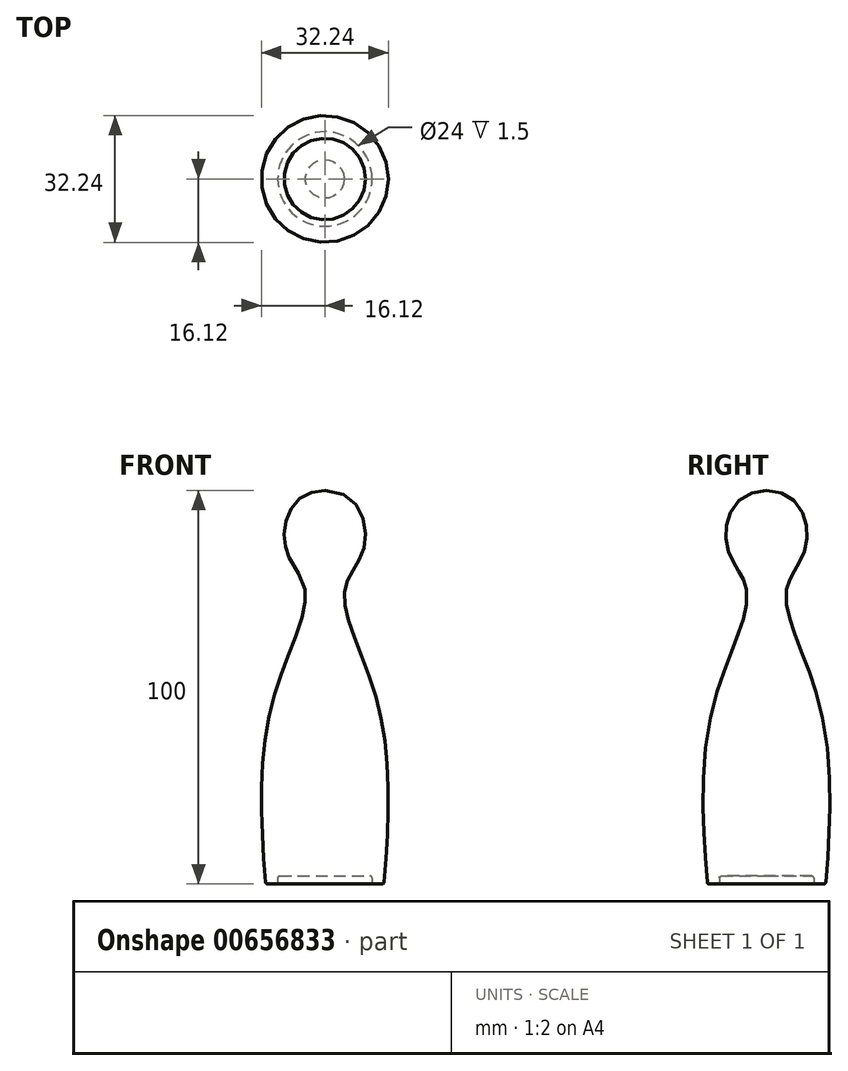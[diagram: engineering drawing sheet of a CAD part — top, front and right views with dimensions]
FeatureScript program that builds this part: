
annotation { "Feature Type Name" : "Feature", "Feature Type Description" : "" }
export const myFeature = defineFeature(function(context is Context, id is Id, definition is map)
    precondition{}
    {
        {
            var Q0;
            Q0=qCreatedBy(makeId("Front.planeOp"),FACE);
            var sketch = newSketch(context, id + "F0", { "sketchPlane" : qUnion([Q0])});
            skLineSegment(sketch, "E0", {"start": v(0, 53.24) * mm, "end": v(0, -46.52) * mm, "construction": true});
            skFitSpline(sketch, "E1", {"points": [v(0, 48.43) * mm, v(10.08, 34.43) * mm, v(5, 22.85) * mm, v(13.2, -4.93) * mm, v(15, -51.57) * mm], "startDerivative": vector(127.18, -1.17) * mm, "endDerivative": vector(-12.23, -138.3) * mm});
            skLineSegment(sketch, "E2", {"start": v(15, -51.57) * mm, "end": v(0, -51.57) * mm});
            skLineSegment(sketch, "E3", {"start": v(0, 48.43) * mm, "end": v(0, -51.57) * mm});
            skPoint(sketch, "E4", {"position": v(15.75, -20.25) * mm});
            skPoint(sketch, "E5", {"position": v(10, 40.23) * mm});
            skSolve(sketch);
        }
        {
            var Q0;
            Q0=makeQuery(id+"F0.imprint","IMPRINT",FACE,{"disambiguationData":[TD([[makeQuery(id+"F0.imprint","IMPRINT",EDGE,{"derivedFrom":sQuery(id+"F0.wireOp",EDGE,"E1")}),-1.0]])]});
            var Q1;
            Q1=sQuery(id+"F0.wireOp",EDGE,"E3");
            revolve(context, id + "F1", {"entities" : qUnion([Q0]), "axis" : qUnion([Q1]), "revolveType" : RevolveType.FULL});
        }
        {
            var Q0;
            Q0=makeQuery(id+"F1.opRevolve","SWEPT_FACE",FACE,{"disambiguationData":[OSD([sQuery(id+"F0.wireOp",EDGE,"E2")])]});
            var sketch = newSketch(context, id + "F2", { "sketchPlane" : qUnion([Q0])});
            skCircle(sketch, "E6", {"center": v(0, 0) * mm, "radius": 12 * mm});
            skSolve(sketch);
        }
        {
            var Q0;
            Q0=makeQuery(id+"F2.imprint","IMPRINT",FACE,{"disambiguationData":[TD([[makeQuery(id+"F2.imprint","IMPRINT",EDGE,{"derivedFrom":sQuery(id+"F2.wireOp",EDGE,"E6")}),1.0]])]});
            var Q1;
            Q1=sQuery(id+"F2.wireOp",EDGE,"E6");
            extrude(context, id + "F3", {"entities" : qUnion([Q0]), "operationType" : NewBodyOperationType.REMOVE, "surfaceEntities" : qUnion([Q1]), "oppositeDirection" : true, "depth" : 2 * mm, "offsetDistance" : 25 * mm});
        }
        {
            var Q0;
            Q0=makeQuery(id+"F3.boolean.opBoolean","COPY",EDGE,{"derivedFrom":makeQuery(id+"F3.opExtrude","CAP_EDGE",EDGE,{"disambiguationData":[OSD([sQuery(id+"F2.wireOp",EDGE,"E6")])],"isStart":true})});
            var Q1;
            Q1=makeQuery(id+"F1.opRevolve","SWEPT_EDGE",EDGE,{"disambiguationData":[OSD([sQuery(id+"F0.wireOp",EDGE,"E1"),sQuery(id+"F0.wireOp",EDGE,"E2")])]});
            var Q2;
            Q2=makeQuery(id+"F3.boolean.opBoolean","COPY",EDGE,{"derivedFrom":makeQuery(id+"F3.opExtrude","CAP_EDGE",EDGE,{"disambiguationData":[OSD([sQuery(id+"F2.wireOp",EDGE,"E6")])],"isStart":false})});
            fillet(context, id + "F4", {"entities" : qUnion([Q0, Q1, Q2]), "radius" : 0.5 * mm, "tangentPropagation" : true, "allowEdgeOverflow" : false});
        }
    });
